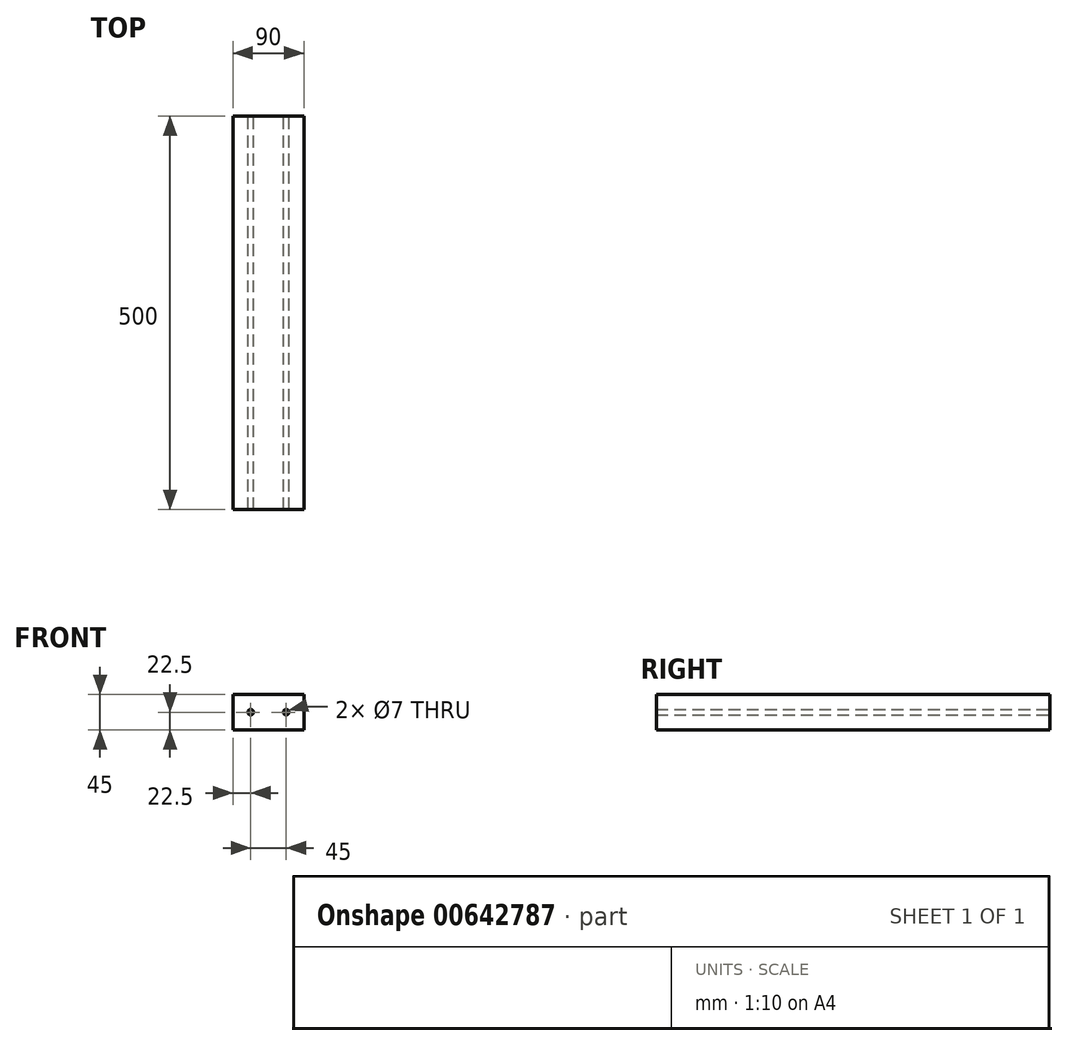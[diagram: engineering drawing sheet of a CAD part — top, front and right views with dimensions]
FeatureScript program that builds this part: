
annotation { "Feature Type Name" : "Feature", "Feature Type Description" : "" }
export const myFeature = defineFeature(function(context is Context, id is Id, definition is map)
    precondition{}
    {
        {
            var Q0;
            Q0=qCreatedBy(makeId("Front.planeOp"),FACE);
            var sketch = newSketch(context, id + "F0", { "sketchPlane" : qUnion([Q0])});
            skLineSegment(sketch, "E0.bottom", {"start": v(0, 0) * mm, "end": v(90, 0) * mm});
            skLineSegment(sketch, "E0.top", {"start": v(0, 45) * mm, "end": v(90, 45) * mm});
            skLineSegment(sketch, "E0.left", {"start": v(0, 0) * mm, "end": v(0, 45) * mm});
            skLineSegment(sketch, "E0.right", {"start": v(90, 0) * mm, "end": v(90, 45) * mm});
            skSolve(sketch);
        }
        {
            var Q0;
            Q0=makeQuery(id+"F0.imprint","IMPRINT",FACE,{"disambiguationData":[TD([[makeQuery(id+"F0.imprint","IMPRINT",EDGE,{"derivedFrom":sQuery(id+"F0.wireOp",EDGE,"E0.bottom")}),1.0]])]});
            extrude(context, id + "F1", {"entities" : qUnion([Q0]), "depth" : 500 * mm, "offsetDistance" : 25 * mm});
        }
        {
            var Q0;
            Q0=makeQuery(id+"F1.opExtrude","CAP_FACE",FACE,{"disambiguationData":[OSD([sQuery(id+"F0.wireOp",EDGE,"E0.bottom"),sQuery(id+"F0.wireOp",EDGE,"E0.top"),sQuery(id+"F0.wireOp",EDGE,"E0.left"),sQuery(id+"F0.wireOp",EDGE,"E0.right")])],"isStart":true});
            var sketch = newSketch(context, id + "F2", { "sketchPlane" : qUnion([Q0])});
            skPoint(sketch, "E1", {"position": v(-67.5, 22.5) * mm});
            skPoint(sketch, "E1.positionSnap0", {"position": v(-90, 22.5) * mm});
            skPoint(sketch, "E2", {"position": v(-22.5, 22.5) * mm});
            skSolve(sketch);
        }
        {
            var Q0;
            Q0=sQuery(id+"F2.wireOp",VERTEX,"E1");
            var Q1;
            Q1=sQuery(id+"F2.wireOp",VERTEX,"E2");
            var Q2;
            Q2=makeQuery(id+"F1.opExtrude","SWEPT_BODY",BODY,{"disambiguationData":[OSD([sQuery(id+"F0.wireOp",EDGE,"E0.bottom"),sQuery(id+"F0.wireOp",EDGE,"E0.top"),sQuery(id+"F0.wireOp",EDGE,"E0.left"),sQuery(id+"F0.wireOp",EDGE,"E0.right")])]});
            hole(context, id + "F3", {"style" : HoleStyle.SIMPLE, "endStyle" : HoleEndStyle.THROUGH, "standardTappedOrClearance" : lookupTablePath({ "standard" : "ISO", "size" : "7", "type" : "Drilled" }), "standardBlindInLast" : lookupTablePath({ "standard" : "ISO", "size" : "7", "type" : "Drilled" }), "holeDiameter" : 7 * mm, "majorDiameter" : 5 * mm, "isTappedThrough" : true, "tappedDepth" : 14.5 * mm, "tapClearance" : 3, "startFromSketch" : true, "locations" : qUnion([Q0, Q1]), "scope" : qUnion([Q2])});
        }
    });
